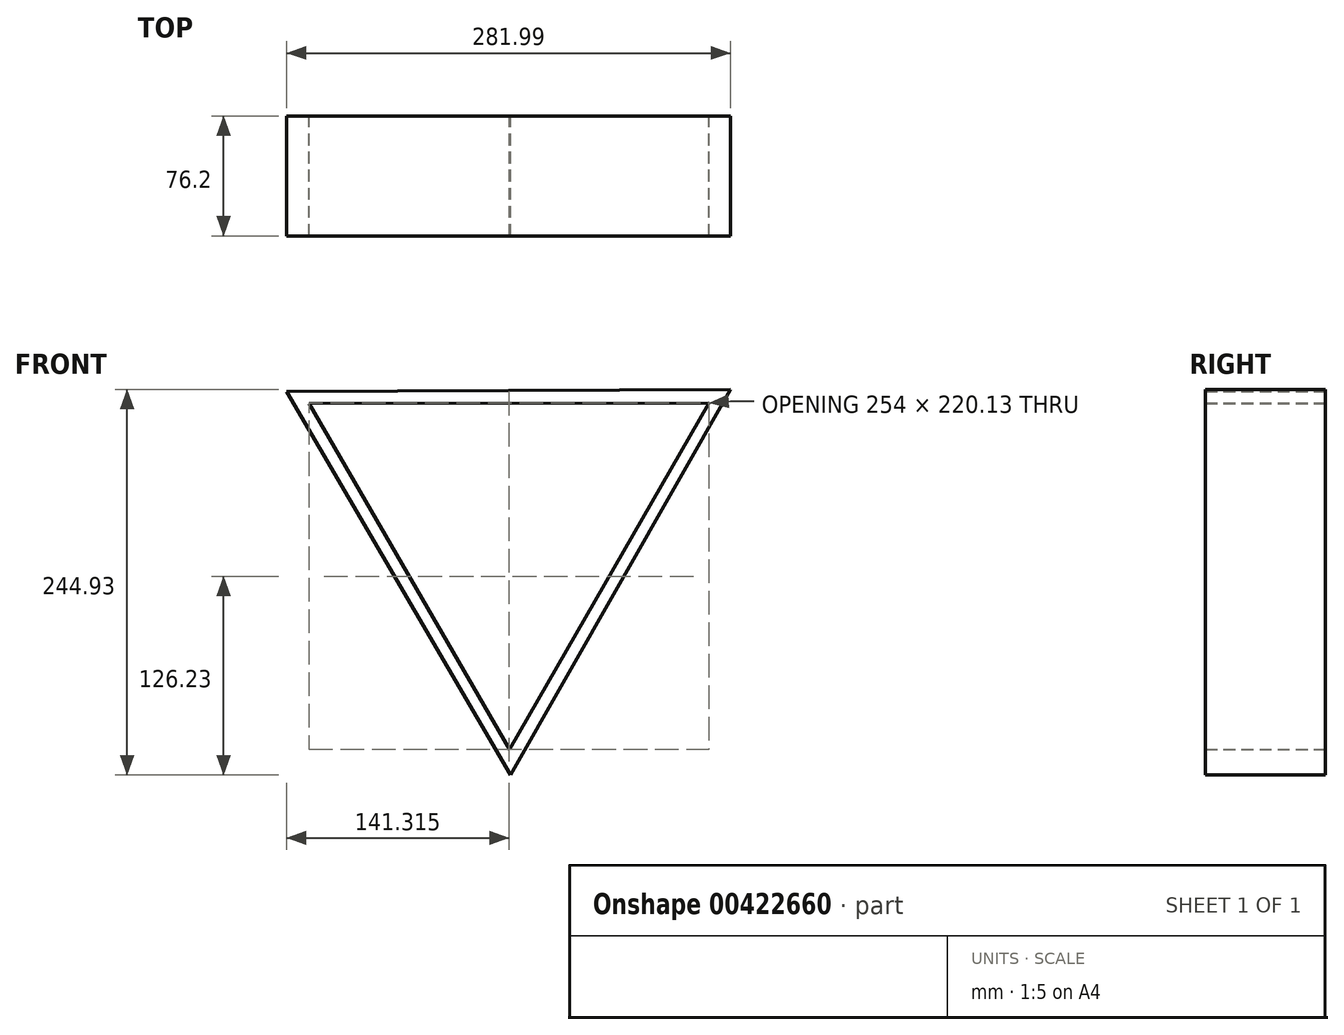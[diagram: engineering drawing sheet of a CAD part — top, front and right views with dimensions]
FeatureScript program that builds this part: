
annotation { "Feature Type Name" : "Feature", "Feature Type Description" : "" }
export const myFeature = defineFeature(function(context is Context, id is Id, definition is map)
    precondition{}
    {
        {
            var Q0;
            Q0=qCreatedBy(makeId("Front.planeOp"),FACE);
            var sketch = newSketch(context, id + "F0", { "sketchPlane" : qUnion([Q0])});
            skCircle(sketch, "E0.cCircle", {"center": v(0, 0) * mm, "radius": 81.4 * mm, "construction": true});
            skLineSegment(sketch, "E0.0", {"start": v(140.58, 82.12) * mm, "end": v(0.83, -162.81) * mm});
            skLineSegment(sketch, "E0.1", {"start": v(0.83, -162.81) * mm, "end": v(-141.41, 80.69) * mm});
            skLineSegment(sketch, "E0.2", {"start": v(-141.41, 80.69) * mm, "end": v(140.58, 82.12) * mm});
            skPoint(sketch, "E0.0.midPoint", {"position": v(70.7, -40.34) * mm});
            skCircle(sketch, "E1.cCircle", {"center": v(0, 0) * mm, "radius": 73.32 * mm, "construction": true});
            skLineSegment(sketch, "E1.0", {"start": v(126.9, 73.49) * mm, "end": v(0.19, -146.65) * mm});
            skLineSegment(sketch, "E1.1", {"start": v(0.19, -146.65) * mm, "end": v(-127.1, 73.16) * mm});
            skLineSegment(sketch, "E1.2", {"start": v(-127.1, 73.16) * mm, "end": v(126.9, 73.49) * mm});
            skPoint(sketch, "E1.0.midPoint", {"position": v(63.55, -36.58) * mm});
            skSolve(sketch);
        }
        {
            var Q0;
            Q0=makeQuery(id+"F0.imprint","IMPRINT",FACE,{"disambiguationData":[TD([[makeQuery(id+"F0.imprint","IMPRINT",EDGE,{"derivedFrom":sQuery(id+"F0.wireOp",EDGE,"E0.0")}),-1.0]])]});
            extrude(context, id + "F1", {"entities" : qUnion([Q0]), "depth" : 76.2 * mm});
        }
    });
